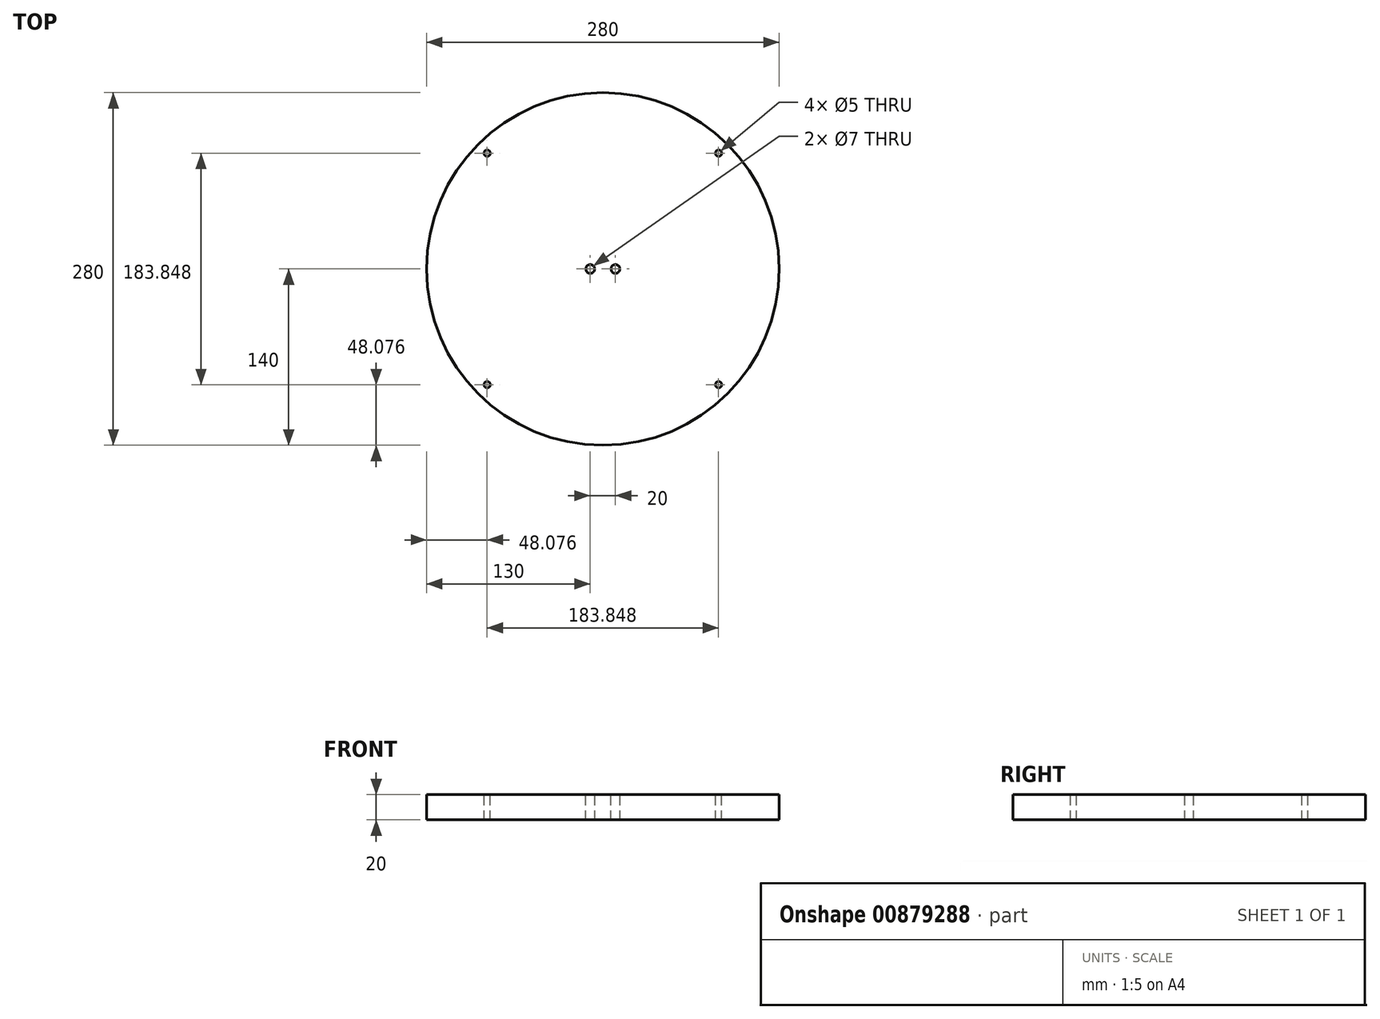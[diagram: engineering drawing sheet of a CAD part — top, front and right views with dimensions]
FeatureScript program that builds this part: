
annotation { "Feature Type Name" : "Feature", "Feature Type Description" : "" }
export const myFeature = defineFeature(function(context is Context, id is Id, definition is map)
    precondition{}
    {
        {
            var Q0;
            Q0=qCreatedBy(makeId("Top.planeOp"),FACE);
            var sketch = newSketch(context, id + "F0", { "sketchPlane" : qUnion([Q0])});
            skCircle(sketch, "E0", {"center": v(0, 0) * mm, "radius": 140 * mm});
            skSolve(sketch);
        }
        {
            var Q0;
            Q0 = qSketchRegion(id + "F0", true);
            extrude(context, id + "F1", {"entities" : qUnion([Q0]), "depth" : 20 * mm, "offsetDistance" : 25 * mm});
        }
        {
            var Q0;
            Q0=makeQuery(id+"F1.opExtrude","CAP_FACE",FACE,{"disambiguationData":[OSD([sQuery(id+"F0.wireOp",EDGE,"E0")])],"isStart":false});
            var sketch = newSketch(context, id + "F2", { "sketchPlane" : qUnion([Q0])});
            skCircle(sketch, "E1", {"center": v(-10, 0) * mm, "radius": 3.5 * mm});
            skCircle(sketch, "E2", {"center": v(10, 0) * mm, "radius": 3.5 * mm});
            skSolve(sketch);
        }
        {
            var Q0;
            Q0=makeQuery(id+"F2.imprint","IMPRINT",FACE,{"disambiguationData":[TD([[makeQuery(id+"F2.imprint","IMPRINT",EDGE,{"derivedFrom":sQuery(id+"F2.wireOp",EDGE,"E1")}),1.0]])]});
            var Q1;
            Q1=makeQuery(id+"F2.imprint","IMPRINT",FACE,{"disambiguationData":[TD([[makeQuery(id+"F2.imprint","IMPRINT",EDGE,{"derivedFrom":sQuery(id+"F2.wireOp",EDGE,"E2")}),1.0]])]});
            extrude(context, id + "F3", {"entities" : qUnion([Q0, Q1]), "operationType" : NewBodyOperationType.REMOVE, "endBound" : BoundingType.THROUGH_ALL, "oppositeDirection" : true, "depth" : 25 * mm, "offsetDistance" : 25 * mm});
        }
        {
            var Q0;
            Q0=makeQuery(id+"F1.opExtrude","CAP_FACE",FACE,{"disambiguationData":[OSD([sQuery(id+"F0.wireOp",EDGE,"E0")])],"isStart":false});
            var sketch = newSketch(context, id + "F4", { "sketchPlane" : qUnion([Q0])});
            skCircle(sketch, "E3", {"center": v(0, 0) * mm, "radius": 130 * mm});
            skLineSegment(sketch, "E4", {"start": v(0, 0) * mm, "end": v(-91.92, 91.92) * mm});
            skLineSegment(sketch, "E5", {"start": v(0, 0) * mm, "end": v(91.92, -91.92) * mm});
            skLineSegment(sketch, "E6", {"start": v(0, 0) * mm, "end": v(-91.92, -91.92) * mm});
            skLineSegment(sketch, "E7", {"start": v(0, 0) * mm, "end": v(91.92, 91.92) * mm});
            skCircle(sketch, "E8", {"center": v(-91.92, 91.92) * mm, "radius": 2.5 * mm});
            skCircle(sketch, "E9", {"center": v(91.92, 91.92) * mm, "radius": 2.5 * mm});
            skCircle(sketch, "E10", {"center": v(91.92, -91.92) * mm, "radius": 2.5 * mm});
            skCircle(sketch, "E11", {"center": v(-91.92, -91.92) * mm, "radius": 2.5 * mm});
            skSolve(sketch);
        }
        {
            var Q0;
            {var subQ0=sQuery(id+"F4.wireOp",EDGE,"E3");var subQ1=makeQuery(id+"F4.imprint","INTERSECT",VERTEX,{"derivedFrom":[subQ0,sQuery(id+"F4.wireOp",EDGE,"E4")]});Q0=makeQuery(id+"F4.imprint","IMPRINT",FACE,{"disambiguationData":[TD([[makeQuery(id+"F4.imprint","IMPRINT",EDGE,{"disambiguationData":[TD([[subQ1,1.0]])],"derivedFrom":subQ0}),-1.0]])]});}
            var Q1;
            {var subQ0=sQuery(id+"F4.wireOp",EDGE,"E4");var subQ1=sQuery(id+"F4.wireOp",EDGE,"E3");var subQ2=makeQuery(id+"F4.imprint","INTERSECT",VERTEX,{"derivedFrom":[subQ1,subQ0]});Q1=makeQuery(id+"F4.imprint","IMPRINT",FACE,{"disambiguationData":[TD([[makeQuery(id+"F4.imprint","IMPRINT",EDGE,{"disambiguationData":[TD([[subQ2,-1.0]])],"derivedFrom":subQ1}),1.0]])]});}
            var Q2;
            {var subQ0=sQuery(id+"F4.wireOp",EDGE,"E4");var subQ1=sQuery(id+"F4.wireOp",EDGE,"E3");var subQ2=makeQuery(id+"F4.imprint","INTERSECT",VERTEX,{"derivedFrom":[subQ1,subQ0]});Q2=makeQuery(id+"F4.imprint","IMPRINT",FACE,{"disambiguationData":[TD([[makeQuery(id+"F4.imprint","IMPRINT",EDGE,{"disambiguationData":[TD([[subQ2,1.0]])],"derivedFrom":subQ1}),1.0]])]});}
            var Q3;
            {var subQ0=sQuery(id+"F4.wireOp",EDGE,"E3");var subQ1=makeQuery(id+"F4.imprint","INTERSECT",VERTEX,{"derivedFrom":[subQ0,sQuery(id+"F4.wireOp",EDGE,"E7")]});Q3=makeQuery(id+"F4.imprint","IMPRINT",FACE,{"disambiguationData":[TD([[makeQuery(id+"F4.imprint","IMPRINT",EDGE,{"disambiguationData":[TD([[subQ1,1.0]])],"derivedFrom":subQ0}),-1.0]])]});}
            var Q4;
            {var subQ0=sQuery(id+"F4.wireOp",EDGE,"E7");var subQ1=sQuery(id+"F4.wireOp",EDGE,"E3");var subQ2=makeQuery(id+"F4.imprint","INTERSECT",VERTEX,{"derivedFrom":[subQ1,subQ0]});Q4=makeQuery(id+"F4.imprint","IMPRINT",FACE,{"disambiguationData":[TD([[makeQuery(id+"F4.imprint","IMPRINT",EDGE,{"disambiguationData":[TD([[subQ2,1.0]])],"derivedFrom":subQ1}),1.0]])]});}
            var Q5;
            {var subQ0=sQuery(id+"F4.wireOp",EDGE,"E7");var subQ1=sQuery(id+"F4.wireOp",EDGE,"E3");var subQ2=makeQuery(id+"F4.imprint","INTERSECT",VERTEX,{"derivedFrom":[subQ1,subQ0]});Q5=makeQuery(id+"F4.imprint","IMPRINT",FACE,{"disambiguationData":[TD([[makeQuery(id+"F4.imprint","IMPRINT",EDGE,{"disambiguationData":[TD([[subQ2,-1.0]])],"derivedFrom":subQ1}),1.0]])]});}
            var Q6;
            {var subQ0=sQuery(id+"F4.wireOp",EDGE,"E3");var subQ1=makeQuery(id+"F4.imprint","INTERSECT",VERTEX,{"derivedFrom":[subQ0,sQuery(id+"F4.wireOp",EDGE,"E6")]});Q6=makeQuery(id+"F4.imprint","IMPRINT",FACE,{"disambiguationData":[TD([[makeQuery(id+"F4.imprint","IMPRINT",EDGE,{"disambiguationData":[TD([[subQ1,1.0]])],"derivedFrom":subQ0}),-1.0]])]});}
            var Q7;
            {var subQ0=sQuery(id+"F4.wireOp",EDGE,"E6");var subQ1=sQuery(id+"F4.wireOp",EDGE,"E3");var subQ2=makeQuery(id+"F4.imprint","INTERSECT",VERTEX,{"derivedFrom":[subQ1,subQ0]});Q7=makeQuery(id+"F4.imprint","IMPRINT",FACE,{"disambiguationData":[TD([[makeQuery(id+"F4.imprint","IMPRINT",EDGE,{"disambiguationData":[TD([[subQ2,1.0]])],"derivedFrom":subQ1}),1.0]])]});}
            var Q8;
            {var subQ0=sQuery(id+"F4.wireOp",EDGE,"E6");var subQ1=sQuery(id+"F4.wireOp",EDGE,"E3");var subQ2=makeQuery(id+"F4.imprint","INTERSECT",VERTEX,{"derivedFrom":[subQ1,subQ0]});Q8=makeQuery(id+"F4.imprint","IMPRINT",FACE,{"disambiguationData":[TD([[makeQuery(id+"F4.imprint","IMPRINT",EDGE,{"disambiguationData":[TD([[subQ2,-1.0]])],"derivedFrom":subQ1}),1.0]])]});}
            var Q9;
            {var subQ0=sQuery(id+"F4.wireOp",EDGE,"E3");var subQ1=makeQuery(id+"F4.imprint","INTERSECT",VERTEX,{"derivedFrom":[subQ0,sQuery(id+"F4.wireOp",EDGE,"E5")]});Q9=makeQuery(id+"F4.imprint","IMPRINT",FACE,{"disambiguationData":[TD([[makeQuery(id+"F4.imprint","IMPRINT",EDGE,{"disambiguationData":[TD([[subQ1,1.0]])],"derivedFrom":subQ0}),-1.0]])]});}
            var Q10;
            {var subQ0=sQuery(id+"F4.wireOp",EDGE,"E5");var subQ1=sQuery(id+"F4.wireOp",EDGE,"E3");var subQ2=makeQuery(id+"F4.imprint","INTERSECT",VERTEX,{"derivedFrom":[subQ1,subQ0]});Q10=makeQuery(id+"F4.imprint","IMPRINT",FACE,{"disambiguationData":[TD([[makeQuery(id+"F4.imprint","IMPRINT",EDGE,{"disambiguationData":[TD([[subQ2,-1.0]])],"derivedFrom":subQ1}),1.0]])]});}
            var Q11;
            {var subQ0=sQuery(id+"F4.wireOp",EDGE,"E5");var subQ1=sQuery(id+"F4.wireOp",EDGE,"E3");var subQ2=makeQuery(id+"F4.imprint","INTERSECT",VERTEX,{"derivedFrom":[subQ1,subQ0]});Q11=makeQuery(id+"F4.imprint","IMPRINT",FACE,{"disambiguationData":[TD([[makeQuery(id+"F4.imprint","IMPRINT",EDGE,{"disambiguationData":[TD([[subQ2,1.0]])],"derivedFrom":subQ1}),1.0]])]});}
            extrude(context, id + "F5", {"entities" : qUnion([Q0, Q1, Q2, Q3, Q4, Q5, Q6, Q7, Q8, Q9, Q10, Q11]), "operationType" : NewBodyOperationType.REMOVE, "oppositeDirection" : true, "depth" : 25 * mm, "offsetDistance" : 25 * mm});
        }
    });
